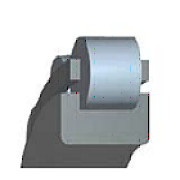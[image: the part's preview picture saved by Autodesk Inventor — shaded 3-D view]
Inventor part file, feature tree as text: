
AUTODESK INVENTOR PART (.ipt)
format: ipt  version: 2022 (Build 260153000, 153)  size: 162,304 bytes
history: native  units: mm (DEFAULTED — no unit token found)
features: other x1, sketch x1
ambient origin geometry x8: Origin, YZ Plane, XZ Plane, XY Plane, X Axis, Y Axis, Z Axis, Center Point
bodies: Solid1 (feature_tree)
feature tree (2):
  other  "轴承体"
  sketch  "草图"  dims[d0=2.5mm d1=2.5mm d2=4.0mm d3=7.0mm d4=90.0deg d5=0.1125mm d6=0.0mm d7=0.0mm d8=0.0mm d9=0.0mm d10=0.0mm]
